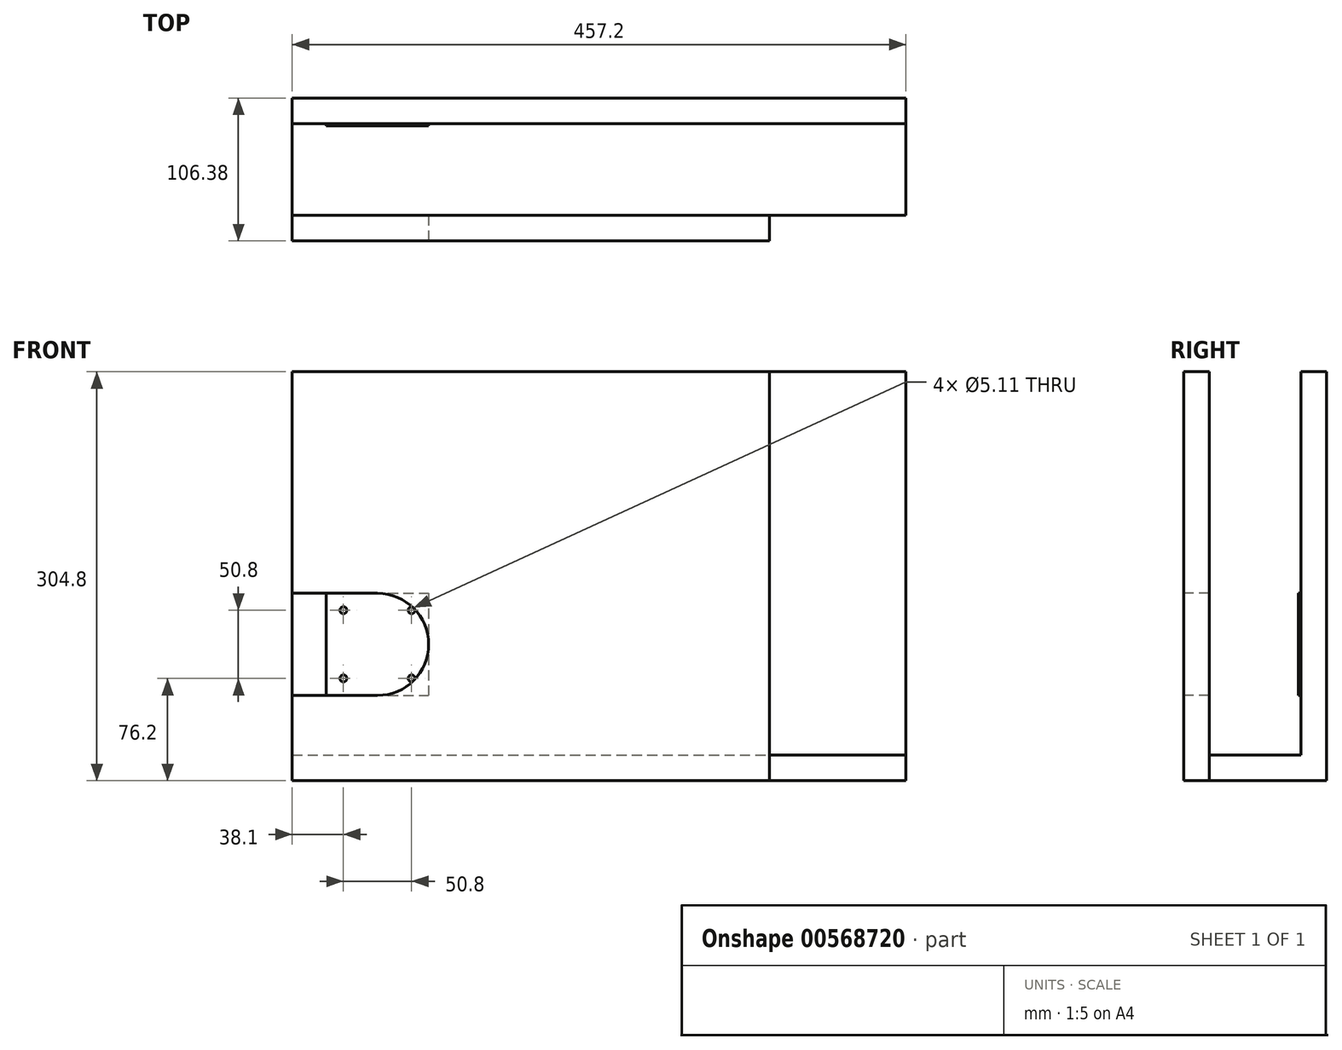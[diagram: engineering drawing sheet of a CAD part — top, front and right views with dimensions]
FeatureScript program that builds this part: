
annotation { "Feature Type Name" : "Feature", "Feature Type Description" : "" }
export const myFeature = defineFeature(function(context is Context, id is Id, definition is map)
    precondition{}
    {
        {
            var Q0;
            Q0=qCreatedBy(makeId("Right.planeOp"),FACE);
            var sketch = newSketch(context, id + "F0", { "sketchPlane" : qUnion([Q0])});
            skLineSegment(sketch, "E0.bottom", {"start": v(-53.19, 152.4) * mm, "end": v(53.19, 152.4) * mm});
            skLineSegment(sketch, "E0.top", {"start": v(-53.19, -152.4) * mm, "end": v(53.19, -152.4) * mm});
            skLineSegment(sketch, "E0.left", {"start": v(-53.19, 152.4) * mm, "end": v(-53.19, -152.4) * mm});
            skLineSegment(sketch, "E0.right", {"start": v(53.19, 152.4) * mm, "end": v(53.19, -152.4) * mm});
            skPoint(sketch, "E0.middle", {"position": v(0, 0) * mm});
            skSolve(sketch);
        }
        {
            var Q0;
            Q0 = qSketchRegion(id + "F0", true);
            extrude(context, id + "F1", {"entities" : qUnion([Q0]), "endBound" : BoundingType.SYMMETRIC, "oppositeDirection" : true, "depth" : 457.2 * mm, "offsetDistance" : 25.4 * mm});
        }
        {
            var Q0;
            Q0=qCreatedBy(makeId("Front.planeOp"),FACE);
            var sketch = newSketch(context, id + "F2", { "sketchPlane" : qUnion([Q0])});
            skLineSegment(sketch, "E1.bottom", {"start": v(127, 152.4) * mm, "end": v(228.6, 152.4) * mm});
            skLineSegment(sketch, "E1.top", {"start": v(127, -152.4) * mm, "end": v(228.6, -152.4) * mm});
            skLineSegment(sketch, "E1.left", {"start": v(127, 152.4) * mm, "end": v(127, -152.4) * mm});
            skLineSegment(sketch, "E1.right", {"start": v(228.6, 152.4) * mm, "end": v(228.6, -152.4) * mm});
            skSolve(sketch);
        }
        {
            var Q0;
            Q0=qCreatedBy(makeId("Right.planeOp"),FACE);
            var sketch = newSketch(context, id + "F3", { "sketchPlane" : qUnion([Q0])});
            skLineSegment(sketch, "E2.bottom", {"start": v(-34.14, 152.4) * mm, "end": v(34.14, 152.4) * mm});
            skLineSegment(sketch, "E2.top", {"start": v(-34.14, -133.35) * mm, "end": v(34.14, -133.35) * mm});
            skLineSegment(sketch, "E2.left", {"start": v(-34.14, 152.4) * mm, "end": v(-34.14, -133.35) * mm});
            skLineSegment(sketch, "E2.right", {"start": v(34.14, 152.4) * mm, "end": v(34.14, -133.35) * mm});
            skSolve(sketch);
        }
        {
            var Q0;
            Q0 = qSketchRegion(id + "F3", true);
            extrude(context, id + "F4", {"entities" : qUnion([Q0]), "operationType" : NewBodyOperationType.REMOVE, "endBound" : BoundingType.SYMMETRIC, "oppositeDirection" : true, "depth" : 457.2 * mm, "offsetDistance" : 25.4 * mm});
        }
        {
            var Q0;
            Q0=makeQuery(id+"F1.opExtrude","SWEPT_FACE",FACE,{"disambiguationData":[OSD([sQuery(id+"F0.wireOp",EDGE,"E0.left")])]});
            var sketch = newSketch(context, id + "F5", { "sketchPlane" : qUnion([Q0])});
            skLineSegment(sketch, "E3.bottom", {"start": v(228.6, 152.4) * mm, "end": v(127, 152.4) * mm});
            skLineSegment(sketch, "E3.top", {"start": v(228.6, -133.35) * mm, "end": v(127, -133.35) * mm});
            skLineSegment(sketch, "E3.left", {"start": v(228.6, 152.4) * mm, "end": v(228.6, -133.35) * mm});
            skLineSegment(sketch, "E3.right", {"start": v(127, 152.4) * mm, "end": v(127, -133.35) * mm});
            skSolve(sketch);
        }
        {
            var Q0;
            Q0 = qSketchRegion(id + "F5", true);
            var Q1;
            Q1=makeQuery(id+"F4.boolean.opBoolean","COPY",FACE,{"derivedFrom":makeQuery(id+"F4.opExtrude","SWEPT_FACE",FACE,{"disambiguationData":[OSD([sQuery(id+"F3.wireOp",EDGE,"E2.left")])]})});
            var Q2;
            Q2=makeQuery(id+"F4.boolean.opBoolean","COPY",VERTEX,{"derivedFrom":makeQuery(id+"F4.opExtrude","CAP_VERTEX",VERTEX,{"disambiguationData":[OSD([sQuery(id+"F3.wireOp",EDGE,"E2.bottom"),sQuery(id+"F3.wireOp",EDGE,"E2.right")])],"isStart":true})});
            extrude(context, id + "F6", {"entities" : qUnion([Q0]), "operationType" : NewBodyOperationType.REMOVE, "endBound" : BoundingType.UP_TO_VERTEX, "oppositeDirection" : true, "depth" : 25.4 * mm, "endBoundEntityFace" : qUnion([Q1]), "endBoundEntityVertex" : qUnion([Q2]), "offsetDistance" : 25.4 * mm});
        }
        {
            var Q0;
            Q0=makeQuery(id+"F4.boolean.opBoolean","COPY",FACE,{"derivedFrom":makeQuery(id+"F4.opExtrude","SWEPT_FACE",FACE,{"disambiguationData":[OSD([sQuery(id+"F3.wireOp",EDGE,"E2.right")])]})});
            var sketch = newSketch(context, id + "F7", { "sketchPlane" : qUnion([Q0])});
            skLineSegment(sketch, "E4.bottom", {"start": v(-203.2, -12.7) * mm, "end": v(-127, -12.7) * mm});
            skLineSegment(sketch, "E4.top", {"start": v(-203.2, -88.9) * mm, "end": v(-127, -88.9) * mm});
            skLineSegment(sketch, "E4.left", {"start": v(-203.2, -12.7) * mm, "end": v(-203.2, -88.9) * mm});
            skLineSegment(sketch, "E4.right", {"start": v(-127, -12.7) * mm, "end": v(-127, -88.9) * mm});
            skPoint(sketch, "E4.middle", {"position": v(-165.1, -50.8) * mm});
            skCircle(sketch, "E5", {"center": v(-190.5, -25.4) * mm, "radius": 2.55 * mm});
            skLineSegment(sketch, "E6", {"start": v(-165.1, -12.7) * mm, "end": v(-165.1, -88.9) * mm, "construction": true});
            skLineSegment(sketch, "E7", {"start": v(-203.2, -50.8) * mm, "end": v(-127, -50.8) * mm, "construction": true});
            skCircle(sketch, "E8.MirrorC", {"center": v(-139.7, -25.4) * mm, "radius": 2.55 * mm});
            skCircle(sketch, "E9.MirrorC", {"center": v(-190.5, -76.2) * mm, "radius": 2.55 * mm});
            skCircle(sketch, "E10.MirrorC", {"center": v(-139.7, -76.2) * mm, "radius": 2.55 * mm});
            skSolve(sketch);
        }
        {
            var Q0;
            Q0 = qSketchRegion(id + "F7", true);
            extrude(context, id + "F8", {"entities" : qUnion([Q0]), "depth" : 1.68 * mm, "offsetDistance" : 25.4 * mm});
        }
        {
            var Q0;
            Q0=makeQuery(id+"F1.opExtrude","SWEPT_FACE",FACE,{"disambiguationData":[OSD([sQuery(id+"F0.wireOp",EDGE,"E0.left")])]});
            var sketch = newSketch(context, id + "F9", { "sketchPlane" : qUnion([Q0])});
            skArc(sketch, "E11", {"start": v(-165.1, -88.9) * mm, "mid": v(-127, -50.8) * mm, "end": v(-165.1, -12.7) * mm});
            skLineSegment(sketch, "E12", {"start": v(-165.1, -12.7) * mm, "end": v(-165.1, -88.9) * mm, "construction": true});
            skLineSegment(sketch, "E13", {"start": v(-165.1, -12.7) * mm, "end": v(-228.6, -12.7) * mm});
            skLineSegment(sketch, "E14", {"start": v(-228.6, -12.7) * mm, "end": v(-228.6, -88.9) * mm});
            skLineSegment(sketch, "E15", {"start": v(-228.6, -88.9) * mm, "end": v(-165.1, -88.9) * mm});
            skSolve(sketch);
        }
        {
            var Q0;
            Q0 = qSketchRegion(id + "F9", true);
            extrude(context, id + "F10", {"entities" : qUnion([Q0]), "operationType" : NewBodyOperationType.REMOVE, "endBound" : BoundingType.UP_TO_NEXT, "oppositeDirection" : true, "depth" : 25.4 * mm, "offsetDistance" : 25.4 * mm});
        }
        {
            var Q0;
            Q0=makeQuery(id+"F6.boolean.opBoolean","MERGE",FACE,{"derivedFrom":[makeQuery(id+"F4.boolean.opBoolean","COPY",FACE,{"derivedFrom":makeQuery(id+"F4.opExtrude","SWEPT_FACE",FACE,{"disambiguationData":[OSD([sQuery(id+"F3.wireOp",EDGE,"E2.top")])]})}),makeQuery(id+"F6.opExtrude","SWEPT_FACE",FACE,{"disambiguationData":[OSD([sQuery(id+"F5.wireOp",EDGE,"E3.top")])]})]});
            var sketch = newSketch(context, id + "F11", { "sketchPlane" : qUnion([Q0])});
            skLineSegment(sketch, "E16.bottom", {"start": v(127, -34.14) * mm, "end": v(228.6, -34.14) * mm});
            skLineSegment(sketch, "E16.top", {"start": v(127, -53.19) * mm, "end": v(228.6, -53.19) * mm});
            skLineSegment(sketch, "E16.left", {"start": v(127, -34.14) * mm, "end": v(127, -53.19) * mm});
            skLineSegment(sketch, "E16.right", {"start": v(228.6, -34.14) * mm, "end": v(228.6, -53.19) * mm});
            skSolve(sketch);
        }
        {
            var Q0;
            Q0 = qSketchRegion(id + "F11", true);
            extrude(context, id + "F12", {"entities" : qUnion([Q0]), "operationType" : NewBodyOperationType.REMOVE, "endBound" : BoundingType.THROUGH_ALL, "oppositeDirection" : true, "depth" : 25.4 * mm, "offsetDistance" : 25.4 * mm});
        }
    });
